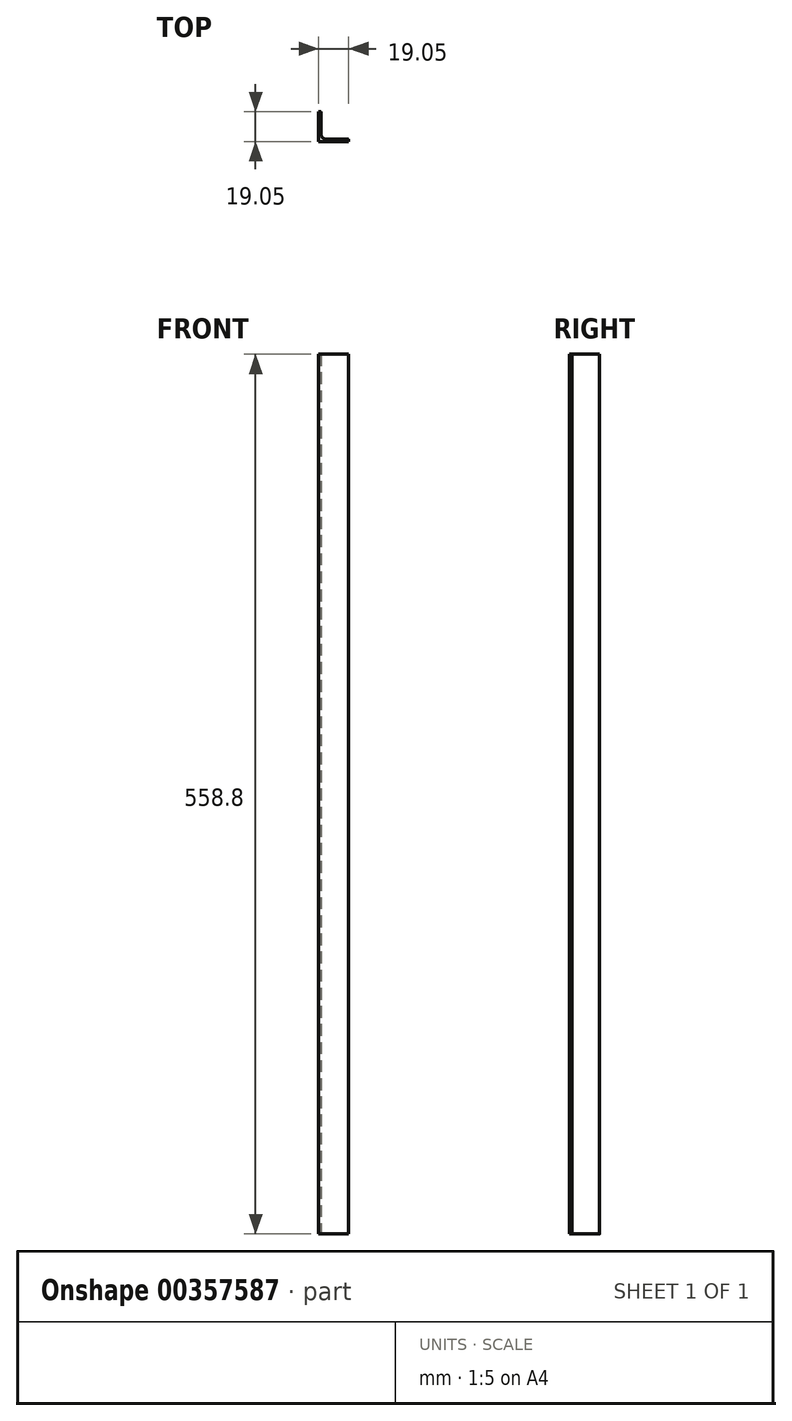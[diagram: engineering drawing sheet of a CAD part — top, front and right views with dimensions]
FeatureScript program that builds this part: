
annotation { "Feature Type Name" : "Feature", "Feature Type Description" : "" }
export const myFeature = defineFeature(function(context is Context, id is Id, definition is map)
    precondition{}
    {
        {
            var Q0;
            Q0=qCreatedBy(makeId("Top.planeOp"),FACE);
            var sketch = newSketch(context, id + "F0", { "sketchPlane" : qUnion([Q0])});
            skLineSegment(sketch, "E0", {"start": v(0, 0) * mm, "end": v(0, 19.05) * mm});
            skLineSegment(sketch, "E1", {"start": v(0, 19.05) * mm, "end": v(1.08, 19.05) * mm});
            skLineSegment(sketch, "E2", {"start": v(1.59, 18.54) * mm, "end": v(1.59, 4.76) * mm});
            skLineSegment(sketch, "E3", {"start": v(4.76, 1.59) * mm, "end": v(18.54, 1.59) * mm});
            skLineSegment(sketch, "E4", {"start": v(19.05, 1.08) * mm, "end": v(19.05, 0) * mm});
            skLineSegment(sketch, "E5", {"start": v(19.05, 0) * mm, "end": v(0, 0) * mm});
            skPoint(sketch, "E6.visualSharp", {"position": v(1.59, 1.59) * mm});
            skArc(sketch, "E6.filletArc", {"start": v(1.59, 4.76) * mm, "mid": v(2.52, 2.52) * mm, "end": v(4.76, 1.59) * mm});
            skPoint(sketch, "E7.visualSharp", {"position": v(19.05, 1.59) * mm});
            skArc(sketch, "E7.filletArc", {"start": v(19.05, 1.08) * mm, "mid": v(18.9, 1.44) * mm, "end": v(18.54, 1.59) * mm});
            skPoint(sketch, "E8.visualSharp", {"position": v(1.59, 19.05) * mm});
            skArc(sketch, "E8.filletArc", {"start": v(1.59, 18.54) * mm, "mid": v(1.44, 18.9) * mm, "end": v(1.08, 19.05) * mm});
            skSolve(sketch);
        }
        {
            var Q0;
            Q0 = qSketchRegion(id + "F0", true);
            extrude(context, id + "F1", {"entities" : qUnion([Q0]), "depth" : 558.8 * mm});
        }
    });
